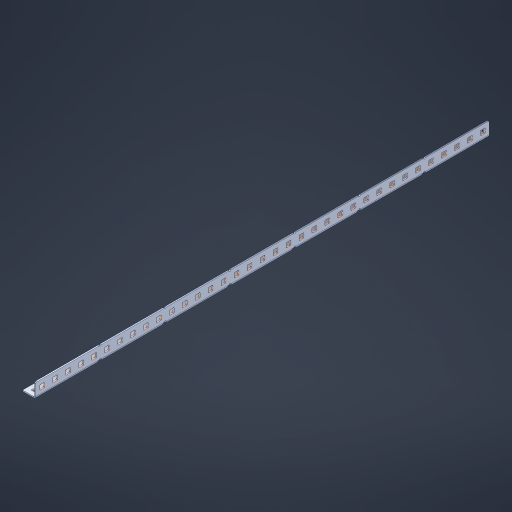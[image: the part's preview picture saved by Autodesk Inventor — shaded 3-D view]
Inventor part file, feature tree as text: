
AUTODESK INVENTOR PART (.ipt)
format: ipt  version: 2023 (Build 270158000, 158)  size: 1,041,408 bytes
history: native  units: in
note: dims shown in document units (in); Inventor stores cm internally (conversion verified against a paired STEP export)
features: other x75, extrude x69, sheet_metal_op x10, sketch x8, mirror x1, pattern_linear x1, chamfer x1
ambient origin geometry x8: Origin, YZ Plane, XZ Plane, XY Plane, X Axis, Y Axis, Z Axis, Center Point
bodies: Solid1 (feature_tree), Body (feature_tree)
feature tree (165):
  other  "Flange Pattern Plane"
  sheet_metal_op  "Flange Pattern"
  sheet_metal_op  "Body Pattern"
  other  "Arc Length"
  mirror  "Notch Mirror"
  pattern_linear  "Notch Pattern"  Spacing1=0.1875in  [1 undecoded]
  chamfer  "End Chamfer"
  extrude  "Half Cut"  Depth=0.0469in
  sketch  "Sketch1"  dims[d0=2.5in]
  other  "Plate1"
  sketch  "Sketch2"  dims[d1=17.5in]
  other  "Plate2"
  sheet_metal_op  "Bend1"
  sheet_metal_op  "Corner1"
  sketch  "Sketch3"  dims[d2=0.0469in]
  other  "Flange Pattern Sketch"
  sketch  "Sketch7"  dims[d3=0.0469in]
  other  "Srf1"
  other  "Srf2"
  sketch  "Sketch8"  dims[d4=0.0234in]
  sketch  "Sketch9"  dims[d5=0.0938in]
  other  "Srf91"
  sheet_metal_op  "Body Pattern Sketch"
  other  "Srf92"
  sketch  "Sketch13"  dims[d6=0.0469in]
  sketch  "Sketch14"  dims[d7=0.5in d8=90.0deg d9=0.0312in d10=0.1875in d11=0.0469in d12=0.0469in d16=0.182in d17=0.02in d18=0.0469in d19=0.0in d20=0.25in d21=0.25in d46=0.172in d47=1.0in d48=0.0in d49=0.182in d50=0.02in d51=0.25in d52=0.25in d53=0.0469in d54=0.0in d55=0.172in d56=1.0in d57=0.0in d60=13.7795in d62=0.5in d63=0.3937in d65=0.5in d85=0.1227in d86=0.1659in d88=0.04in d89=0.0469in d90=0.0in d91=0.04in d92=0.0491in d95=2.5in d96=0.04in d97=0.25in d98=45.0deg d101=0.0in d102=2.497in d131=0.5in d132=13.7795in d134=0.5in d139=0.5in]
  other  "Srf856"
  other  "Srf1310"
  other  "Srf1311"
  other  "Srf1312"
  other  "Srf1376"
  other  "Srf1377"
  other  "Srf1728"
  other  "Srf1755"
  other  "Srf1878"
  other  "Srf1879"
  other  "Srf1880"
  other  "Srf1881"
  other  "Srf1882"
  other  "Srf1883"
  other  "Srf1884"
  other  "Srf1885"
  other  "Srf1886"
  other  "Srf1887"
  other  "Srf1888"
  other  "Srf1889"
  other  "Srf1890"
  other  "Srf1891"
  other  "Srf1892"
  other  "Srf1893"
  other  "Srf1894"
  other  "Srf1895"
  other  "Srf1896"
  other  "Srf1897"
  other  "Srf1898"
  other  "Srf1899"
  other  "Srf1900"
  other  "Srf1901"
  other  "Srf1902"
  other  "Srf1903"
  other  "Srf1904"
  other  "Srf1905"
  other  "Srf1906"
  other  "Srf1942"
  other  "Srf1943"
  other  "Srf1944"
  other  "Srf1945"
  other  "Srf1946"
  other  "Srf1947"
  other  "Srf1948"
  other  "Srf1949"
  other  "Srf1950"
  other  "Srf1951"
  other  "Srf1952"
  other  "Srf1953"
  other  "Srf1954"
  other  "Srf1955"
  other  "Srf1956"
  other  "Srf1957"
  other  "Srf1958"
  other  "Srf1959"
  other  "Srf1960"
  other  "Srf1961"
  other  "Srf1962"
  other  "Srf1963"
  other  "Srf1964"
  other  "Srf1965"
  other  "Srf1966"
  other  "Srf1967"
  other  "Srf1968"
  other  "Srf1969"
  other  "Srf1970"
  sheet_metal_op  "Flange Stamp"
  sheet_metal_op  "Flange Circle"
  sheet_metal_op  "Body Stamp"
  sheet_metal_op  "Body Circle"
  sheet_metal_op  "Notch"
  extrude  "ExtrusionSrf2"  Depth=0.0469in
  extrude  "ExtrusionSrf92"  Depth=0.5in
  extrude  "ExtrusionSrf856"  Depth=0.02in
  extrude  "ExtrusionSrf1310"  Depth=0.0469in
  extrude  "ExtrusionSrf1311"  TaperAngle=0.0deg  [1 undecoded]
  extrude  "ExtrusionSrf1312"  Depth=0.5in
  extrude  "ExtrusionSrf1376"  Depth=0.5in
  extrude  "ExtrusionSrf1377"  Depth=0.5in
  extrude  "ExtrusionSrf1728"  Depth=0.5in TaperAngle=0.0deg
  extrude  "ExtrusionSrf1755"  Depth=0.5in
  extrude  "ExtrusionSrf1878"  Depth=0.02in
  extrude  "ExtrusionSrf1879"  Depth=0.5in
  extrude  "ExtrusionSrf1880"  Depth=0.5in
  extrude  "ExtrusionSrf1881"  Depth=0.0469in
  extrude  "ExtrusionSrf1882"  TaperAngle=0.0deg  [1 undecoded]
  extrude  "ExtrusionSrf1883"  Depth=0.5in
  extrude  "ExtrusionSrf1884"  Depth=0.5in TaperAngle=0.0deg
  extrude  "ExtrusionSrf1885"  Depth=0.5in
  extrude  "ExtrusionSrf1886"  Depth=0.5in
  extrude  "ExtrusionSrf1887"  Depth=0.5in
  extrude  "ExtrusionSrf1888"  Depth=0.5in
  extrude  "ExtrusionSrf1889"  Depth=0.5in
  extrude  "ExtrusionSrf1890"  Depth=0.0469in
  extrude  "ExtrusionSrf1891"  TaperAngle=0.0deg  [1 undecoded]
  extrude  "ExtrusionSrf1892"  Depth=0.5in
  extrude  "ExtrusionSrf1893"  Depth=0.5in
  extrude  "ExtrusionSrf1894"  Depth=0.5in
  extrude  "ExtrusionSrf1895"  Depth=0.5in TaperAngle=45.0deg
  extrude  "ExtrusionSrf1896"  TaperAngle=0.0deg  [1 undecoded]
  extrude  "ExtrusionSrf1897"  Depth=0.5in
  extrude  "ExtrusionSrf1898"  Depth=0.5in
  extrude  "ExtrusionSrf1899"  Depth=0.5in
  extrude  "ExtrusionSrf1900"  Depth=0.5in
  extrude  "ExtrusionSrf1901"  Depth=0.5in
  extrude  "ExtrusionSrf1902"  [1 undecoded]
  extrude  "ExtrusionSrf1903"  [1 undecoded]
  extrude  "ExtrusionSrf1904"  [1 undecoded]
  extrude  "ExtrusionSrf1905"  [1 undecoded]
  extrude  "ExtrusionSrf1906"  [1 undecoded]
  extrude  "ExtrusionSrf1942"  [1 undecoded]
  extrude  "ExtrusionSrf1943"  [1 undecoded]
  extrude  "ExtrusionSrf1944"  [1 undecoded]
  extrude  "ExtrusionSrf1945"  [1 undecoded]
  extrude  "ExtrusionSrf1946"  [1 undecoded]
  extrude  "ExtrusionSrf1947"  [1 undecoded]
  extrude  "ExtrusionSrf1948"  [1 undecoded]
  extrude  "ExtrusionSrf1949"  [1 undecoded]
  extrude  "ExtrusionSrf1950"  [1 undecoded]
  extrude  "ExtrusionSrf1951"  [1 undecoded]
  extrude  "ExtrusionSrf1952"  [1 undecoded]
  extrude  "ExtrusionSrf1953"  [1 undecoded]
  extrude  "ExtrusionSrf1954"  [1 undecoded]
  extrude  "ExtrusionSrf1955"  [1 undecoded]
  extrude  "ExtrusionSrf1956"  [1 undecoded]
  extrude  "ExtrusionSrf1957"  [1 undecoded]
  extrude  "ExtrusionSrf1958"  [1 undecoded]
  extrude  "ExtrusionSrf1959"  [1 undecoded]
  extrude  "ExtrusionSrf1960"  [1 undecoded]
  extrude  "ExtrusionSrf1961"  [1 undecoded]
  extrude  "ExtrusionSrf1962"  [1 undecoded]
  extrude  "ExtrusionSrf1963"  [1 undecoded]
  extrude  "ExtrusionSrf1964"  [1 undecoded]
  extrude  "ExtrusionSrf1965"  [1 undecoded]
  extrude  "ExtrusionSrf1966"  [1 undecoded]
  extrude  "ExtrusionSrf1967"  [1 undecoded]
  extrude  "ExtrusionSrf1968"  [1 undecoded]
  extrude  "ExtrusionSrf1969"  [1 undecoded]
  extrude  "ExtrusionSrf1970"  [1 undecoded]
note: 39 required parameter values undecoded (feature->parameter linkage not recoverable at this tier; creation-order binding heuristic only, values carry confidence <= 0.55)
